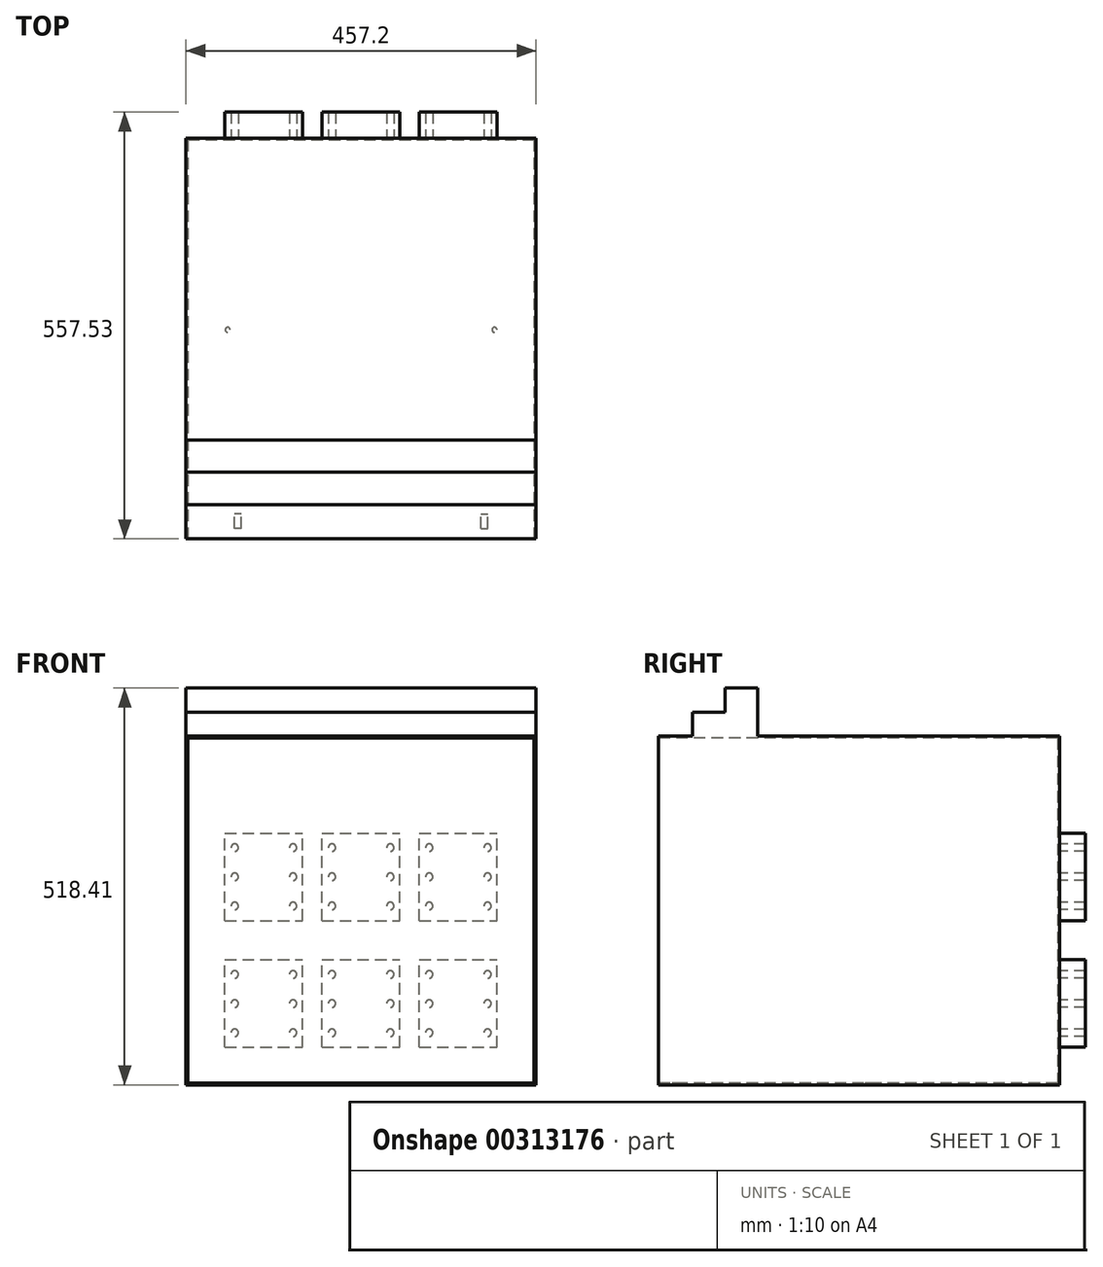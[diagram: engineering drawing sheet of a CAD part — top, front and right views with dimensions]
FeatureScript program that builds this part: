
annotation { "Feature Type Name" : "Feature", "Feature Type Description" : "" }
export const myFeature = defineFeature(function(context is Context, id is Id, definition is map)
    precondition{}
    {
        {
            var Q0;
            Q0=qCreatedBy(makeId("Right.planeOp"),FACE);
            var sketch = newSketch(context, id + "F0", { "sketchPlane" : qUnion([Q0])});
            skLineSegment(sketch, "E0.bottom", {"start": v(261.75, 227.71) * mm, "end": v(-261.75, 227.71) * mm});
            skLineSegment(sketch, "E0.top", {"start": v(261.75, -227.71) * mm, "end": v(-261.75, -227.71) * mm});
            skLineSegment(sketch, "E0.left", {"start": v(261.75, 227.71) * mm, "end": v(261.75, -227.71) * mm});
            skLineSegment(sketch, "E0.right", {"start": v(-261.75, 227.71) * mm, "end": v(-261.75, -227.71) * mm});
            skPoint(sketch, "E0.middle", {"position": v(0, 0) * mm});
            skSolve(sketch);
        }
        {
            var Q0;
            Q0 = qSketchRegion(id + "F0", true);
            extrude(context, id + "F1", {"entities" : qUnion([Q0]), "endBound" : BoundingType.SYMMETRIC, "depth" : 457.2 * mm});
        }
        {
            var Q0;
            Q0=makeQuery(id+"F1.opExtrude","SWEPT_FACE",FACE,{"disambiguationData":[OSD([sQuery(id+"F0.wireOp",EDGE,"E0.right")])]});
            shell(context, id + "F2", {"entities" : qUnion([Q0]), "thickness" : 2.54 * mm});
        }
        {
            var Q0;
            Q0=makeQuery(id+"F1.opExtrude","SWEPT_FACE",FACE,{"disambiguationData":[OSD([sQuery(id+"F0.wireOp",EDGE,"E0.left")])]});
            var sketch = newSketch(context, id + "F3", { "sketchPlane" : qUnion([Q0])});
            skLineSegment(sketch, "E1.bottom", {"start": v(177.8, -178.69) * mm, "end": v(76.2, -178.69) * mm});
            skLineSegment(sketch, "E1.top", {"start": v(177.8, -64.39) * mm, "end": v(76.2, -64.39) * mm});
            skLineSegment(sketch, "E1.left", {"start": v(177.8, -178.69) * mm, "end": v(177.8, -64.39) * mm});
            skLineSegment(sketch, "E1.right", {"start": v(76.2, -178.69) * mm, "end": v(76.2, -64.39) * mm});
            skCircle(sketch, "E2", {"center": v(165.1, -159.64) * mm, "radius": 4.76 * mm});
            skCircle(sketch, "E3.0.1.0", {"center": v(165.1, -121.54) * mm, "radius": 4.76 * mm});
            skCircle(sketch, "E3.0.2.0", {"center": v(165.1, -83.44) * mm, "radius": 4.76 * mm});
            skCircle(sketch, "E3.1.0.0", {"center": v(88.9, -159.64) * mm, "radius": 4.76 * mm});
            skCircle(sketch, "E3.1.1.0", {"center": v(88.9, -121.54) * mm, "radius": 4.76 * mm});
            skCircle(sketch, "E3.1.2.0", {"center": v(88.9, -83.44) * mm, "radius": 4.76 * mm});
            skLineSegment(sketch, "E3.direction1", {"start": v(165.1, -159.64) * mm, "end": v(88.9, -159.64) * mm, "construction": true});
            skLineSegment(sketch, "E3.direction2", {"start": v(165.1, -159.64) * mm, "end": v(165.1, -121.54) * mm, "construction": true});
            skLineSegment(sketch, "E4.0.1.0", {"start": v(76.2, -13.08) * mm, "end": v(76.2, 101.22) * mm});
            skLineSegment(sketch, "E4.0.1.1", {"start": v(177.8, -13.08) * mm, "end": v(177.8, 101.22) * mm});
            skLineSegment(sketch, "E4.0.1.2", {"start": v(177.8, 101.22) * mm, "end": v(76.2, 101.22) * mm});
            skLineSegment(sketch, "E4.0.1.3", {"start": v(165.1, 5.97) * mm, "end": v(88.9, 5.97) * mm, "construction": true});
            skLineSegment(sketch, "E4.0.1.4", {"start": v(165.1, 5.97) * mm, "end": v(165.1, 44.07) * mm, "construction": true});
            skLineSegment(sketch, "E4.0.1.5", {"start": v(177.8, -13.08) * mm, "end": v(76.2, -13.08) * mm});
            skCircle(sketch, "E4.0.1.6", {"center": v(165.1, 82.17) * mm, "radius": 4.76 * mm});
            skCircle(sketch, "E4.0.1.7", {"center": v(88.9, 44.07) * mm, "radius": 4.76 * mm});
            skCircle(sketch, "E4.0.1.8", {"center": v(88.9, 82.17) * mm, "radius": 4.76 * mm});
            skCircle(sketch, "E4.0.1.9", {"center": v(165.1, 44.07) * mm, "radius": 4.76 * mm});
            skCircle(sketch, "E4.0.1.10", {"center": v(88.9, 5.97) * mm, "radius": 4.76 * mm});
            skCircle(sketch, "E4.0.1.11", {"center": v(165.1, 5.97) * mm, "radius": 4.76 * mm});
            skLineSegment(sketch, "E4.1.0.0", {"start": v(-50.8, -178.69) * mm, "end": v(-50.8, -64.39) * mm});
            skLineSegment(sketch, "E4.1.0.1", {"start": v(50.8, -178.69) * mm, "end": v(50.8, -64.39) * mm});
            skLineSegment(sketch, "E4.1.0.2", {"start": v(50.8, -64.39) * mm, "end": v(-50.8, -64.39) * mm});
            skLineSegment(sketch, "E4.1.0.3", {"start": v(38.1, -159.64) * mm, "end": v(-38.1, -159.64) * mm, "construction": true});
            skLineSegment(sketch, "E4.1.0.4", {"start": v(38.1, -159.64) * mm, "end": v(38.1, -121.54) * mm, "construction": true});
            skLineSegment(sketch, "E4.1.0.5", {"start": v(50.8, -178.69) * mm, "end": v(-50.8, -178.69) * mm});
            skCircle(sketch, "E4.1.0.6", {"center": v(38.1, -83.44) * mm, "radius": 4.76 * mm});
            skCircle(sketch, "E4.1.0.7", {"center": v(-38.1, -121.54) * mm, "radius": 4.76 * mm});
            skCircle(sketch, "E4.1.0.8", {"center": v(-38.1, -83.44) * mm, "radius": 4.76 * mm});
            skCircle(sketch, "E4.1.0.9", {"center": v(38.1, -121.54) * mm, "radius": 4.76 * mm});
            skCircle(sketch, "E4.1.0.10", {"center": v(-38.1, -159.64) * mm, "radius": 4.76 * mm});
            skCircle(sketch, "E4.1.0.11", {"center": v(38.1, -159.64) * mm, "radius": 4.76 * mm});
            skLineSegment(sketch, "E4.1.1.0", {"start": v(-50.8, -13.08) * mm, "end": v(-50.8, 101.22) * mm});
            skLineSegment(sketch, "E4.1.1.1", {"start": v(50.8, -13.08) * mm, "end": v(50.8, 101.22) * mm});
            skLineSegment(sketch, "E4.1.1.2", {"start": v(50.8, 101.22) * mm, "end": v(-50.8, 101.22) * mm});
            skLineSegment(sketch, "E4.1.1.3", {"start": v(38.1, 5.97) * mm, "end": v(-38.1, 5.97) * mm, "construction": true});
            skLineSegment(sketch, "E4.1.1.4", {"start": v(38.1, 5.97) * mm, "end": v(38.1, 44.07) * mm, "construction": true});
            skLineSegment(sketch, "E4.1.1.5", {"start": v(50.8, -13.08) * mm, "end": v(-50.8, -13.08) * mm});
            skCircle(sketch, "E4.1.1.6", {"center": v(38.1, 82.17) * mm, "radius": 4.76 * mm});
            skCircle(sketch, "E4.1.1.7", {"center": v(-38.1, 44.07) * mm, "radius": 4.76 * mm});
            skCircle(sketch, "E4.1.1.8", {"center": v(-38.1, 82.17) * mm, "radius": 4.76 * mm});
            skCircle(sketch, "E4.1.1.9", {"center": v(38.1, 44.07) * mm, "radius": 4.76 * mm});
            skCircle(sketch, "E4.1.1.10", {"center": v(-38.1, 5.97) * mm, "radius": 4.76 * mm});
            skCircle(sketch, "E4.1.1.11", {"center": v(38.1, 5.97) * mm, "radius": 4.76 * mm});
            skLineSegment(sketch, "E4.2.0.0", {"start": v(-177.8, -178.69) * mm, "end": v(-177.8, -64.39) * mm});
            skLineSegment(sketch, "E4.2.0.1", {"start": v(-76.2, -178.69) * mm, "end": v(-76.2, -64.39) * mm});
            skLineSegment(sketch, "E4.2.0.2", {"start": v(-76.2, -64.39) * mm, "end": v(-177.8, -64.39) * mm});
            skLineSegment(sketch, "E4.2.0.3", {"start": v(-88.9, -159.64) * mm, "end": v(-165.1, -159.64) * mm, "construction": true});
            skLineSegment(sketch, "E4.2.0.4", {"start": v(-88.9, -159.64) * mm, "end": v(-88.9, -121.54) * mm, "construction": true});
            skLineSegment(sketch, "E4.2.0.5", {"start": v(-76.2, -178.69) * mm, "end": v(-177.8, -178.69) * mm});
            skCircle(sketch, "E4.2.0.6", {"center": v(-88.9, -83.44) * mm, "radius": 4.76 * mm});
            skCircle(sketch, "E4.2.0.7", {"center": v(-165.1, -121.54) * mm, "radius": 4.76 * mm});
            skCircle(sketch, "E4.2.0.8", {"center": v(-165.1, -83.44) * mm, "radius": 4.76 * mm});
            skCircle(sketch, "E4.2.0.9", {"center": v(-88.9, -121.54) * mm, "radius": 4.76 * mm});
            skCircle(sketch, "E4.2.0.10", {"center": v(-165.1, -159.64) * mm, "radius": 4.76 * mm});
            skCircle(sketch, "E4.2.0.11", {"center": v(-88.9, -159.64) * mm, "radius": 4.76 * mm});
            skLineSegment(sketch, "E4.2.1.0", {"start": v(-177.8, -13.08) * mm, "end": v(-177.8, 101.22) * mm});
            skLineSegment(sketch, "E4.2.1.1", {"start": v(-76.2, -13.08) * mm, "end": v(-76.2, 101.22) * mm});
            skLineSegment(sketch, "E4.2.1.2", {"start": v(-76.2, 101.22) * mm, "end": v(-177.8, 101.22) * mm});
            skLineSegment(sketch, "E4.2.1.3", {"start": v(-88.9, 5.97) * mm, "end": v(-165.1, 5.97) * mm, "construction": true});
            skLineSegment(sketch, "E4.2.1.4", {"start": v(-88.9, 5.97) * mm, "end": v(-88.9, 44.07) * mm, "construction": true});
            skLineSegment(sketch, "E4.2.1.5", {"start": v(-76.2, -13.08) * mm, "end": v(-177.8, -13.08) * mm});
            skCircle(sketch, "E4.2.1.6", {"center": v(-88.9, 82.17) * mm, "radius": 4.76 * mm});
            skCircle(sketch, "E4.2.1.7", {"center": v(-165.1, 44.07) * mm, "radius": 4.76 * mm});
            skCircle(sketch, "E4.2.1.8", {"center": v(-165.1, 82.17) * mm, "radius": 4.76 * mm});
            skCircle(sketch, "E4.2.1.9", {"center": v(-88.9, 44.07) * mm, "radius": 4.76 * mm});
            skCircle(sketch, "E4.2.1.10", {"center": v(-165.1, 5.97) * mm, "radius": 4.76 * mm});
            skCircle(sketch, "E4.2.1.11", {"center": v(-88.9, 5.97) * mm, "radius": 4.76 * mm});
            skLineSegment(sketch, "E4.direction1", {"start": v(76.2, -178.69) * mm, "end": v(-50.8, -178.69) * mm, "construction": true});
            skLineSegment(sketch, "E4.direction2", {"start": v(76.2, -178.69) * mm, "end": v(76.2, -13.08) * mm, "construction": true});
            skSolve(sketch);
        }
        {
            var Q0;
            Q0 = qSketchRegion(id + "F3", true);
            extrude(context, id + "F4", {"entities" : qUnion([Q0]), "operationType" : NewBodyOperationType.ADD, "depth" : 34.04 * mm});
        }
        {
            var Q0;
            Q0=makeQuery(id+"F1.opExtrude","SWEPT_FACE",FACE,{"disambiguationData":[OSD([sQuery(id+"F0.wireOp",EDGE,"E0.top")])]});
            var sketch = newSketch(context, id + "F5", { "sketchPlane" : qUnion([Q0])});
            skLineSegment(sketch, "E5.bottom", {"start": v(156.46, 248.28) * mm, "end": v(165.35, 248.28) * mm});
            skLineSegment(sketch, "E5.top", {"start": v(156.46, 229.23) * mm, "end": v(165.35, 229.23) * mm});
            skLineSegment(sketch, "E5.left", {"start": v(156.46, 248.28) * mm, "end": v(156.46, 229.23) * mm});
            skLineSegment(sketch, "E5.right", {"start": v(165.35, 248.28) * mm, "end": v(165.35, 229.23) * mm});
            skLineSegment(sketch, "E6.bottom", {"start": v(-156.46, 248.28) * mm, "end": v(-165.35, 248.28) * mm});
            skLineSegment(sketch, "E6.top", {"start": v(-156.46, 229.23) * mm, "end": v(-165.35, 229.23) * mm});
            skLineSegment(sketch, "E6.left", {"start": v(-156.46, 248.28) * mm, "end": v(-156.46, 229.23) * mm});
            skLineSegment(sketch, "E6.right", {"start": v(-165.35, 248.28) * mm, "end": v(-165.35, 229.23) * mm});
            skCircle(sketch, "E7", {"center": v(174.24, -11.3) * mm, "radius": 3.18 * mm});
            skCircle(sketch, "E8", {"center": v(-174.24, -11.3) * mm, "radius": 3.18 * mm});
            skSolve(sketch);
        }
        {
            var Q0;
            Q0 = qSketchRegion(id + "F5", true);
            extrude(context, id + "F6", {"entities" : qUnion([Q0]), "operationType" : NewBodyOperationType.REMOVE, "endBound" : BoundingType.UP_TO_NEXT, "oppositeDirection" : true, "depth" : 25.4 * mm});
        }
        {
            var Q0;
            Q0=makeQuery(id+"F1.opExtrude","CAP_FACE",FACE,{"disambiguationData":[OSD([sQuery(id+"F0.wireOp",EDGE,"E0.bottom"),sQuery(id+"F0.wireOp",EDGE,"E0.top"),sQuery(id+"F0.wireOp",EDGE,"E0.left"),sQuery(id+"F0.wireOp",EDGE,"E0.right")])],"isStart":false});
            var sketch = newSketch(context, id + "F7", { "sketchPlane" : qUnion([Q0])});
            skLineSegment(sketch, "E9", {"start": v(-217.3, 227.71) * mm, "end": v(-217.3, 259.2) * mm});
            skLineSegment(sketch, "E10", {"start": v(-217.3, 259.2) * mm, "end": v(-174.88, 259.2) * mm});
            skLineSegment(sketch, "E11", {"start": v(-174.88, 259.2) * mm, "end": v(-174.88, 290.7) * mm});
            skLineSegment(sketch, "E12", {"start": v(-174.88, 290.7) * mm, "end": v(-132.46, 290.7) * mm});
            skLineSegment(sketch, "E13", {"start": v(-132.46, 290.7) * mm, "end": v(-132.46, 227.71) * mm});
            skSolve(sketch);
        }
        {
            var Q0;
            {var subQ0=sQuery(id+"F7.wireOp",EDGE,"E9");Q0=makeQuery(id+"F7.imprint","IMPRINT",FACE,{"disambiguationData":[TD([[makeQuery(id+"F7.imprint","IMPRINT",EDGE,{"derivedFrom":subQ0}),-1.0]])]});}
            var Q1;
            Q1=makeQuery(id+"F1.opExtrude","CAP_FACE",FACE,{"disambiguationData":[OSD([sQuery(id+"F0.wireOp",EDGE,"E0.bottom"),sQuery(id+"F0.wireOp",EDGE,"E0.top"),sQuery(id+"F0.wireOp",EDGE,"E0.left"),sQuery(id+"F0.wireOp",EDGE,"E0.right")])],"isStart":true});
            extrude(context, id + "F8", {"entities" : qUnion([Q0]), "operationType" : NewBodyOperationType.ADD, "endBound" : BoundingType.UP_TO_SURFACE, "oppositeDirection" : true, "depth" : 25.4 * mm, "endBoundEntityFace" : qUnion([Q1]), "offsetDistance" : 25.4 * mm});
        }
    });
